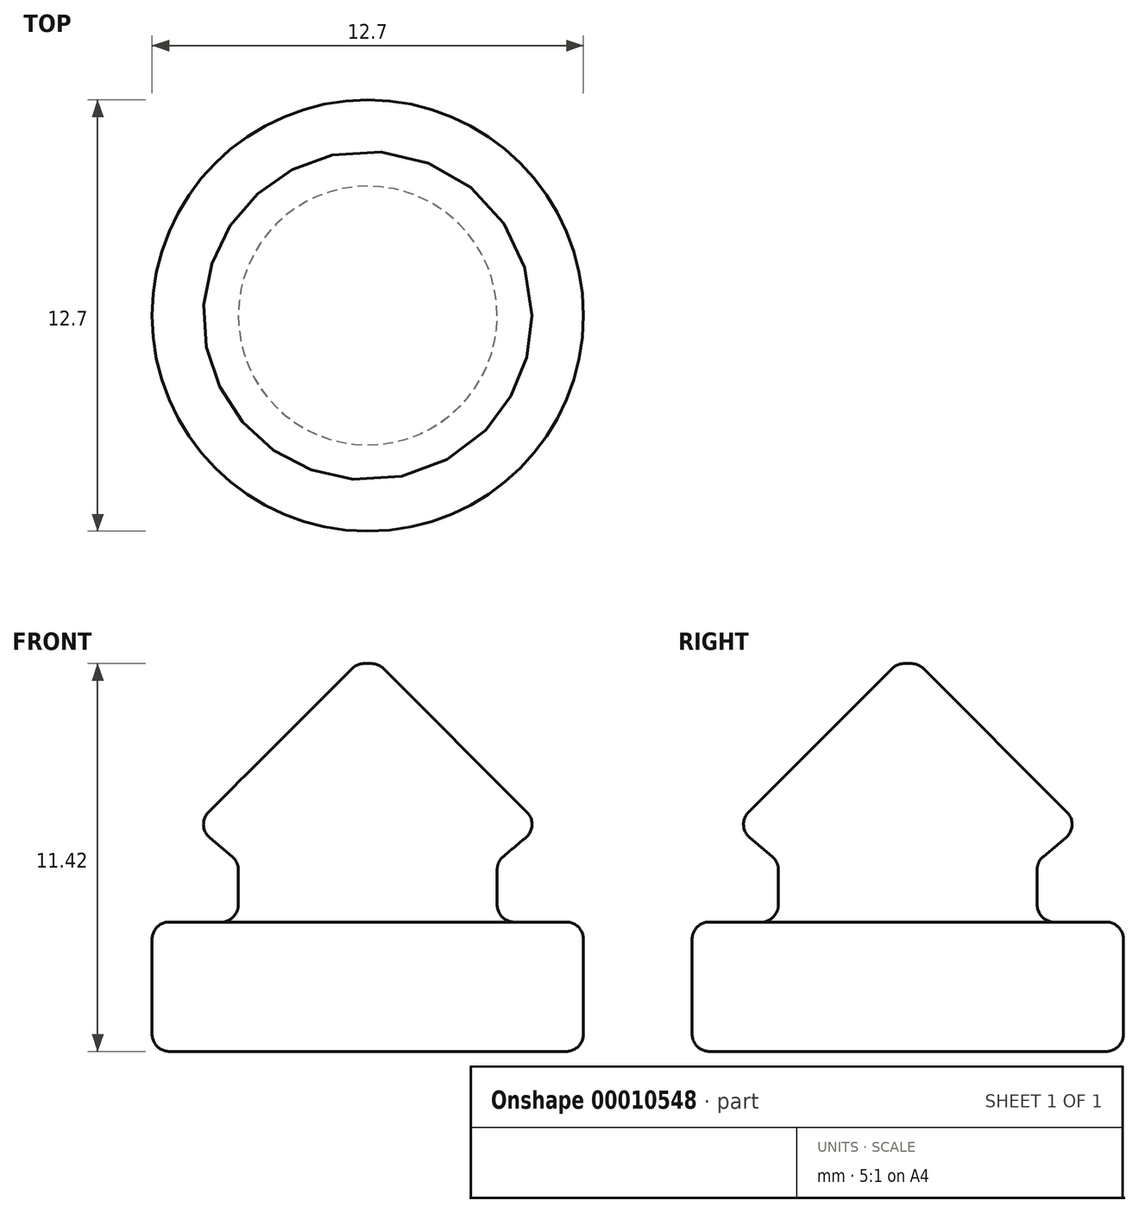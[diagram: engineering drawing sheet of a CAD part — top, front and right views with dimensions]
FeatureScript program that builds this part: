
annotation { "Feature Type Name" : "Feature", "Feature Type Description" : "" }
export const myFeature = defineFeature(function(context is Context, id is Id, definition is map)
    precondition{}
    {
        {
            var Q0;
            Q0=qCreatedBy(makeId("Front.planeOp"),FACE);
            var sketch = newSketch(context, id + "F0", { "sketchPlane" : qUnion([Q0])});
            skLineSegment(sketch, "E0", {"start": v(0, 0) * mm, "end": v(6.35, 0) * mm});
            skLineSegment(sketch, "E1", {"start": v(6.35, 0) * mm, "end": v(6.35, 3.81) * mm});
            skLineSegment(sketch, "E2", {"start": v(6.35, 3.81) * mm, "end": v(3.81, 3.8) * mm});
            skLineSegment(sketch, "E3", {"start": v(3.81, 3.8) * mm, "end": v(3.81, 5.59) * mm});
            skLineSegment(sketch, "E4", {"start": v(3.8, 5.59) * mm, "end": v(5.08, 6.65) * mm});
            skLineSegment(sketch, "E5", {"start": v(5.08, 6.65) * mm, "end": v(0.31, 11.42) * mm});
            skLineSegment(sketch, "E6", {"start": v(0, 0) * mm, "end": v(0, 22.84) * mm, "construction": true});
            skLineSegment(sketch, "E7", {"start": v(0, 11.42) * mm, "end": v(0, 0) * mm});
            skLineSegment(sketch, "E8", {"start": v(0, 11.42) * mm, "end": v(0.31, 11.42) * mm});
            skPoint(sketch, "E9.orphan", {"position": v(0, 11.73) * mm});
            skSolve(sketch);
        }
        {
            var Q0;
            Q0 = qSketchRegion(id + "F0", true);
            var Q1;
            Q1=sQuery(id+"F0.wireOp",EDGE,"E6");
            revolve(context, id + "F1", {"entities" : qUnion([Q0]), "axis" : qUnion([Q1]), "revolveType" : RevolveType.FULL});
        }
        {
            var Q0;
            Q0=makeQuery(id+"F1.opRevolve","SWEPT_FACE",FACE,{"disambiguationData":[OSD([sQuery(id+"F0.wireOp",EDGE,"E5")])]});
            var Q1;
            Q1=makeQuery(id+"F1.opRevolve","SWEPT_FACE",FACE,{"disambiguationData":[OSD([sQuery(id+"F0.wireOp",EDGE,"E1")])]});
            var Q2;
            Q2=makeQuery(id+"F1.opRevolve","SWEPT_FACE",FACE,{"disambiguationData":[OSD([sQuery(id+"F0.wireOp",EDGE,"E3")])]});
            fillet(context, id + "F2", {"entities" : qUnion([Q0, Q1, Q2]), "radius" : 0.5 * mm, "tangentPropagation" : true, "allowEdgeOverflow" : false});
        }
    });
